# Revit family: Haworth_Epure_LinkingDesk_EU_PRELIMINARY
name_source: partatom
category: Furniture
units: mm (PartAtom-declared; Revit-internal decimal feet)

## family parameters
Always vertical = Yes
Cut with Voids When Loaded = No
OmniClass Number = 23.40.70.14.64.11
OmniClass Title = Office Furniture
Room Calculation Point = No
Shared = No
Work Plane-Based = No

## types (8) — shared parameters
Actual Height = 73 cm
Assembly Code = E2020200
Description = Haworth - Epure - Linking Desk
Leg Height = 70 cm
Manufacturer = Haworth
Model = EULXX00X
Revision Number = 1
Size = Verify Final Dim.w/ Haworth
URL = https://www.haworth.com
URL - Product = https://www.haworth.com
Warranty = http://www.haworth.com

## per-type parameters (varying)
| type | 104 x 60 - rounded | 104 x 60 - squared | 138 x 80 - rounded | 138 x 80 - squared | 60 x 60 - rounded | 60 x 60 - squared | 80 x 80 - rounded | 80 x 80 - squared | Actual Depth | Actual Width | Rounded Corners | Squared Corners |
| 60 x 60 - 90 Deg - rounded | No | No | No | No | Yes | No | No | No | 60 cm | 60 cm | Yes | No |
| 60 x 60 - 90 Deg - squared | No | No | No | No | No | Yes | No | No | 60 cm | 60 cm | No | Yes |
| 80 x 80 - 90 Deg - rounded | No | No | No | No | No | No | Yes | No | 80 cm | 80 cm | Yes | No |
| 80 x 80 - 90 Deg - squared | No | No | No | No | No | No | No | Yes | 80 cm | 80 cm | No | Yes |
| 104 x 60 - 120 Deg - rounded | Yes | No | No | No | No | No | No | No | 60 cm | 104 cm | Yes | No |
| 104 x 60 - 120 Deg - squared | No | Yes | No | No | No | No | No | No | 60 cm | 104 cm | No | Yes |
| 138 x 80 - 120 Deg - rounded | No | No | Yes | No | No | No | No | No | 80 cm | 138 cm | Yes | No |
| 138 x 80 - 120 Deg - squared | No | No | No | Yes | No | No | No | No | 80 cm | 138 cm | No | Yes |

## geometry (parser evidence)
native form markers: Sweep x4
no freeform markers — native parametric forms only
